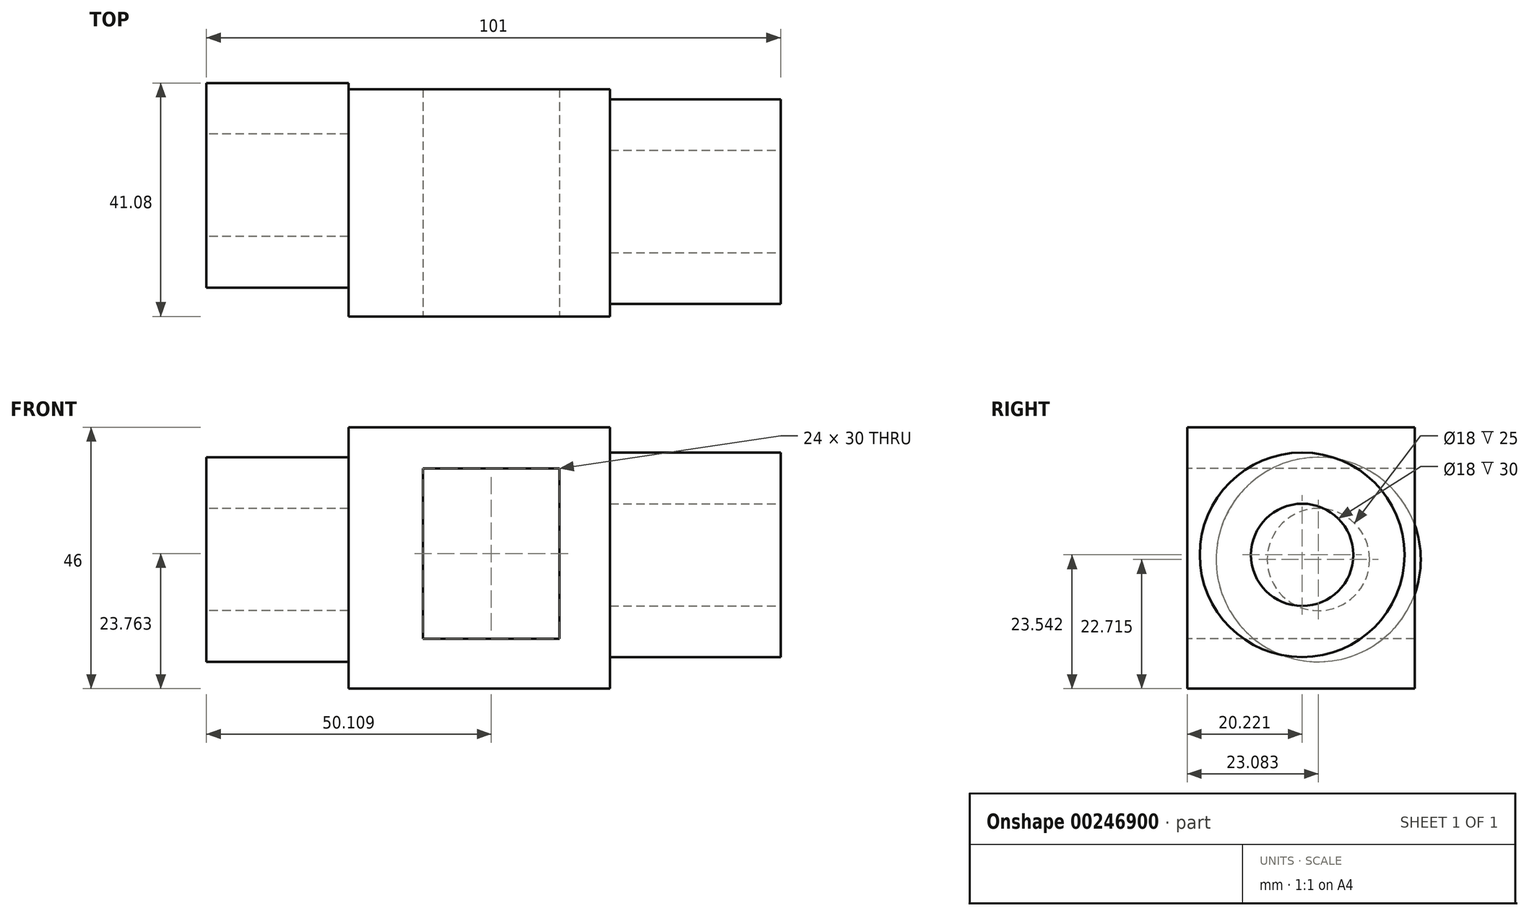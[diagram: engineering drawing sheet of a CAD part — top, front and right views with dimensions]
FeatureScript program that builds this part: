
annotation { "Feature Type Name" : "Feature", "Feature Type Description" : "" }
export const myFeature = defineFeature(function(context is Context, id is Id, definition is map)
    precondition{}
    {
        {
            var Q0;
            Q0=qCreatedBy(makeId("Top.planeOp"),FACE);
            var sketch = newSketch(context, id + "F0", { "sketchPlane" : qUnion([Q0])});
            skLineSegment(sketch, "E0.bottom", {"start": v(-53.67, -58.79) * mm, "end": v(-7.67, -58.79) * mm});
            skLineSegment(sketch, "E0.top", {"start": v(-53.67, -18.79) * mm, "end": v(-7.67, -18.79) * mm});
            skLineSegment(sketch, "E0.left", {"start": v(-53.67, -58.79) * mm, "end": v(-53.67, -18.79) * mm});
            skLineSegment(sketch, "E0.right", {"start": v(-7.67, -58.79) * mm, "end": v(-7.67, -18.79) * mm});
            skSolve(sketch);
        }
        {
            var Q0;
            Q0 = qSketchRegion(id + "F0", true);
            extrude(context, id + "F1", {"entities" : qUnion([Q0]), "depth" : 46 * mm});
        }
        {
            var Q0;
            Q0=makeQuery(id+"F1.opExtrude","SWEPT_FACE",FACE,{"disambiguationData":[OSD([sQuery(id+"F0.wireOp",EDGE,"E0.left")])]});
            var sketch = newSketch(context, id + "F2", { "sketchPlane" : qUnion([Q0])});
            skCircle(sketch, "E1", {"center": v(35.7, 22.71) * mm, "radius": 9 * mm});
            skSolve(sketch);
        }
        {
            var Q0;
            Q0 = qSketchRegion(id + "F2", true);
            extrude(context, id + "F3", {"entities" : qUnion([Q0]), "operationType" : NewBodyOperationType.ADD, "depth" : 30 * mm});
        }
        {
            var Q0;
            Q0=makeQuery(id+"F1.opExtrude","SWEPT_FACE",FACE,{"disambiguationData":[OSD([sQuery(id+"F0.wireOp",EDGE,"E0.right")])]});
            var sketch = newSketch(context, id + "F4", { "sketchPlane" : qUnion([Q0])});
            skCircle(sketch, "E2", {"center": v(-38.57, 23.54) * mm, "radius": 9 * mm});
            skSolve(sketch);
        }
        {
            var Q0;
            Q0 = qSketchRegion(id + "F4", true);
            extrude(context, id + "F5", {"entities" : qUnion([Q0]), "operationType" : NewBodyOperationType.ADD, "depth" : 30 * mm});
        }
        {
            var Q0;
            Q0=makeQuery(id+"F1.opExtrude","SWEPT_FACE",FACE,{"disambiguationData":[OSD([sQuery(id+"F0.wireOp",EDGE,"E0.bottom")])]});
            var sketch = newSketch(context, id + "F6", { "sketchPlane" : qUnion([Q0])});
            skLineSegment(sketch, "E3.bottom", {"start": v(-40.56, 38.76) * mm, "end": v(-16.56, 38.76) * mm});
            skLineSegment(sketch, "E3.top", {"start": v(-40.56, 8.76) * mm, "end": v(-16.56, 8.76) * mm});
            skLineSegment(sketch, "E3.left", {"start": v(-40.56, 38.76) * mm, "end": v(-40.56, 8.76) * mm});
            skLineSegment(sketch, "E3.right", {"start": v(-16.56, 38.76) * mm, "end": v(-16.56, 8.76) * mm});
            skSolve(sketch);
        }
        {
            var Q0;
            Q0 = qSketchRegion(id + "F6", true);
            extrude(context, id + "F7", {"entities" : qUnion([Q0]), "operationType" : NewBodyOperationType.REMOVE, "oppositeDirection" : true, "depth" : 46 * mm});
        }
        {
            var Q0;
            Q0=makeQuery(id+"F3.opExtrude","CAP_FACE",FACE,{"disambiguationData":[OSD([sQuery(id+"F2.wireOp",EDGE,"E1")])],"isStart":false});
            var sketch = newSketch(context, id + "F8", { "sketchPlane" : qUnion([Q0])});
            skSolve(sketch);
        }
        {
            var Q0;
            Q0=makeQuery(id+"F1.opExtrude","SWEPT_FACE",FACE,{"disambiguationData":[OSD([sQuery(id+"F0.wireOp",EDGE,"E0.left")])]});
            var sketch = newSketch(context, id + "F9", { "sketchPlane" : qUnion([Q0])});
            skCircle(sketch, "E4", {"center": v(35.7, 22.71) * mm, "radius": 18 * mm});
            skSolve(sketch);
        }
        {
            var Q0;
            Q0 = qSketchRegion(id + "F9", true);
            extrude(context, id + "F10", {"entities" : qUnion([Q0]), "operationType" : NewBodyOperationType.ADD, "depth" : 25 * mm});
        }
        {
            var Q0;
            Q0=makeQuery(id+"F8.imprint","IMPRINT",FACE,{"disambiguationData":[TD([[makeQuery(id+"F8.imprint","IMPRINT",EDGE,{"derivedFrom":makeQuery(id+"F3.opExtrude","CAP_EDGE",EDGE,{"disambiguationData":[OSD([sQuery(id+"F2.wireOp",EDGE,"E1")])],"isStart":false})}),1.0]])]});
            extrude(context, id + "F11", {"entities" : qUnion([Q0]), "operationType" : NewBodyOperationType.REMOVE, "oppositeDirection" : true, "depth" : 30 * mm});
        }
        {
            var Q0;
            Q0=makeQuery(id+"F1.opExtrude","SWEPT_FACE",FACE,{"disambiguationData":[OSD([sQuery(id+"F0.wireOp",EDGE,"E0.right")])]});
            var sketch = newSketch(context, id + "F12", { "sketchPlane" : qUnion([Q0])});
            skCircle(sketch, "E5", {"center": v(-38.57, 23.54) * mm, "radius": 18 * mm});
            skSolve(sketch);
        }
        {
            var Q0;
            Q0 = qSketchRegion(id + "F12", true);
            extrude(context, id + "F13", {"entities" : qUnion([Q0]), "operationType" : NewBodyOperationType.ADD, "depth" : 30 * mm});
        }
        {
            var Q0;
            Q0=makeQuery(id+"F13.boolean.opBoolean","MERGE",FACE,{"derivedFrom":[makeQuery(id+"F5.opExtrude","CAP_FACE",FACE,{"disambiguationData":[OSD([sQuery(id+"F4.wireOp",EDGE,"E2")])],"isStart":false}),makeQuery(id+"F13.opExtrude","CAP_FACE",FACE,{"disambiguationData":[OSD([sQuery(id+"F12.wireOp",EDGE,"E5")])],"isStart":false})]});
            var sketch = newSketch(context, id + "F14", { "sketchPlane" : qUnion([Q0])});
            skCircle(sketch, "E6", {"center": v(-38.57, 23.54) * mm, "radius": 9 * mm});
            skSolve(sketch);
        }
        {
            var Q0;
            Q0 = qSketchRegion(id + "F14", true);
            extrude(context, id + "F15", {"entities" : qUnion([Q0]), "operationType" : NewBodyOperationType.REMOVE, "oppositeDirection" : true, "depth" : 30 * mm});
        }
    });
